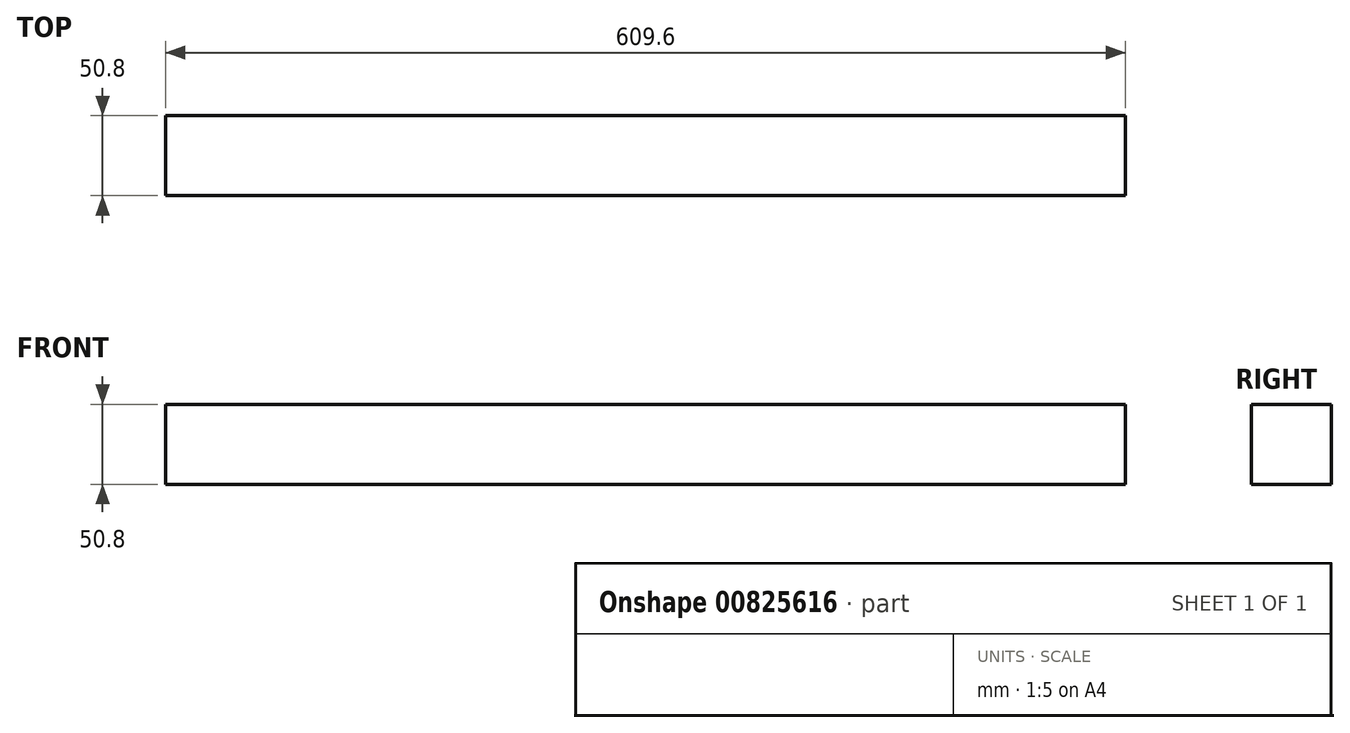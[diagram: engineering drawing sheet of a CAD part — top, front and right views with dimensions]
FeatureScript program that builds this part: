
annotation { "Feature Type Name" : "Feature", "Feature Type Description" : "" }
export const myFeature = defineFeature(function(context is Context, id is Id, definition is map)
    precondition{}
    {
        {
            var Q0;
            Q0=qCreatedBy(makeId("Right.planeOp"),FACE);
            var sketch = newSketch(context, id + "F0", { "sketchPlane" : qUnion([Q0])});
            skLineSegment(sketch, "E0.bottom", {"start": v(-24.58, -17.45) * mm, "end": v(26.22, -17.45) * mm});
            skLineSegment(sketch, "E0.top", {"start": v(-24.58, 33.35) * mm, "end": v(26.22, 33.35) * mm});
            skLineSegment(sketch, "E0.left", {"start": v(-24.58, -17.45) * mm, "end": v(-24.58, 33.35) * mm});
            skLineSegment(sketch, "E0.right", {"start": v(26.22, -17.45) * mm, "end": v(26.22, 33.35) * mm});
            skSolve(sketch);
        }
        {
            var Q0;
            Q0=makeQuery(id+"F0.imprint","IMPRINT",FACE,{"disambiguationData":[TD([[makeQuery(id+"F0.imprint","IMPRINT",EDGE,{"derivedFrom":sQuery(id+"F0.wireOp",EDGE,"E0.bottom")}),1.0]])]});
            extrude(context, id + "F1", {"entities" : qUnion([Q0]), "depth" : 609.6 * mm, "offsetDistance" : 25.4 * mm});
        }
    });
